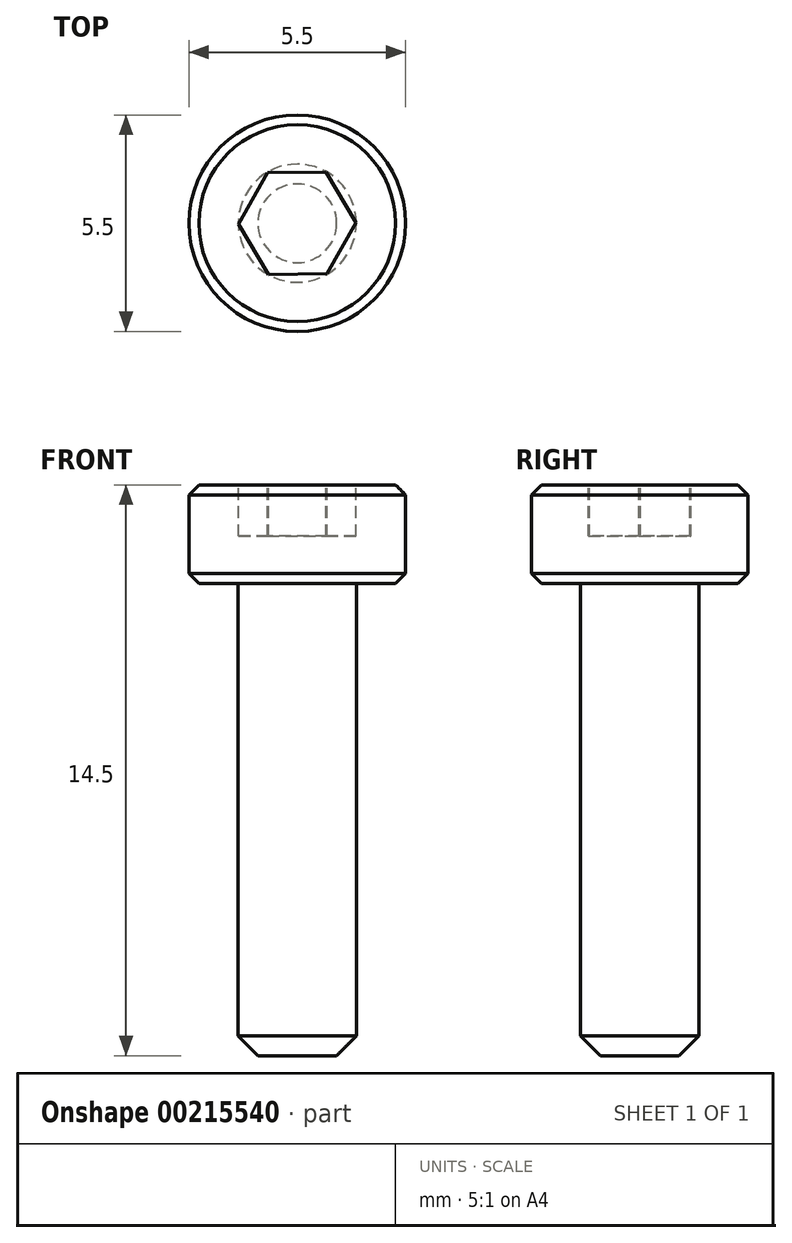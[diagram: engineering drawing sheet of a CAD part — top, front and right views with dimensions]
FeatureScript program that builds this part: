
annotation { "Feature Type Name" : "Feature", "Feature Type Description" : "" }
export const myFeature = defineFeature(function(context is Context, id is Id, definition is map)
    precondition{}
    {
        {
            var Q0;
            Q0=qCreatedBy(makeId("Top.planeOp"),FACE);
            var sketch = newSketch(context, id + "F0", { "sketchPlane" : qUnion([Q0])});
            skCircle(sketch, "E0", {"center": v(0, 0) * mm, "radius": 1.5 * mm});
            skCircle(sketch, "E1", {"center": v(0, 0) * mm, "radius": 2.75 * mm});
            skSolve(sketch);
        }
        {
            var Q0;
            Q0=makeQuery(id+"F0.imprint","IMPRINT",FACE,{"disambiguationData":[TD([[makeQuery(id+"F0.imprint","IMPRINT",EDGE,{"derivedFrom":sQuery(id+"F0.wireOp",EDGE,"E0")}),1.0]])]});
            extrude(context, id + "F1", {"entities" : qUnion([Q0]), "oppositeDirection" : true, "depth" : 12 * mm});
        }
        {
            var Q0;
            Q0=makeQuery(id+"F1.opExtrude","CAP_EDGE",EDGE,{"disambiguationData":[OSD([sQuery(id+"F0.wireOp",EDGE,"E0")])],"isStart":false});
            chamfer(context, id + "F2", {"entities" : qUnion([Q0]), "width" : .5 * mm, "tangentPropagation" : true});
        }
        {
            var Q0;
            Q0=makeQuery(id+"F0.imprint","IMPRINT",FACE,{"disambiguationData":[TD([[makeQuery(id+"F0.imprint","IMPRINT",EDGE,{"derivedFrom":sQuery(id+"F0.wireOp",EDGE,"E0")}),-1.0]])]});
            var Q1;
            Q1=makeQuery(id+"F0.imprint","IMPRINT",FACE,{"disambiguationData":[TD([[makeQuery(id+"F0.imprint","IMPRINT",EDGE,{"derivedFrom":sQuery(id+"F0.wireOp",EDGE,"E0")}),1.0]])]});
            extrude(context, id + "F3", {"entities" : qUnion([Q0, Q1]), "operationType" : NewBodyOperationType.ADD, "depth" : 2.5 * mm});
        }
        {
            var Q0;
            Q0=makeQuery(id+"F3.opExtrude","CAP_FACE",FACE,{"disambiguationData":[OSD([sQuery(id+"F0.wireOp",EDGE,"E1")])],"isStart":false});
            var Q1;
            Q1=makeQuery(id+"F3.opExtrude","CAP_EDGE",EDGE,{"disambiguationData":[OSD([sQuery(id+"F0.wireOp",EDGE,"E1")])],"isStart":true});
            chamfer(context, id + "F4", {"entities" : qUnion([Q0, Q1]), "width" : .25 * mm, "tangentPropagation" : true});
        }
        {
            var Q0;
            Q0=makeQuery(id+"F3.opExtrude","CAP_FACE",FACE,{"disambiguationData":[OSD([sQuery(id+"F0.wireOp",EDGE,"E1")])],"isStart":false});
            var sketch = newSketch(context, id + "F5", { "sketchPlane" : qUnion([Q0])});
            skCircle(sketch, "E2.cCircle", {"center": v(0, 0) * mm, "radius": 1.29 * mm, "construction": true});
            skLineSegment(sketch, "E2.0", {"start": v(1.49, 0.02) * mm, "end": v(0.76, -1.28) * mm});
            skLineSegment(sketch, "E2.1", {"start": v(0.76, -1.28) * mm, "end": v(-0.73, -1.3) * mm});
            skLineSegment(sketch, "E2.2", {"start": v(-0.73, -1.3) * mm, "end": v(-1.49, -0.02) * mm});
            skLineSegment(sketch, "E2.3", {"start": v(-1.49, -0.02) * mm, "end": v(-0.76, 1.28) * mm});
            skLineSegment(sketch, "E2.4", {"start": v(-0.76, 1.28) * mm, "end": v(0.73, 1.3) * mm});
            skLineSegment(sketch, "E2.5", {"start": v(0.73, 1.3) * mm, "end": v(1.49, 0.02) * mm});
            skPoint(sketch, "E2.0.midPoint", {"position": v(1.12, -0.63) * mm});
            skSolve(sketch);
        }
        {
            var Q0;
            Q0=qSketchRegion(id+"F5",true);
            extrude(context, id + "F6", {"entities" : qUnion([Q0]), "operationType" : NewBodyOperationType.REMOVE, "oppositeDirection" : true, "depth" : 1.3 * mm});
        }
    });
